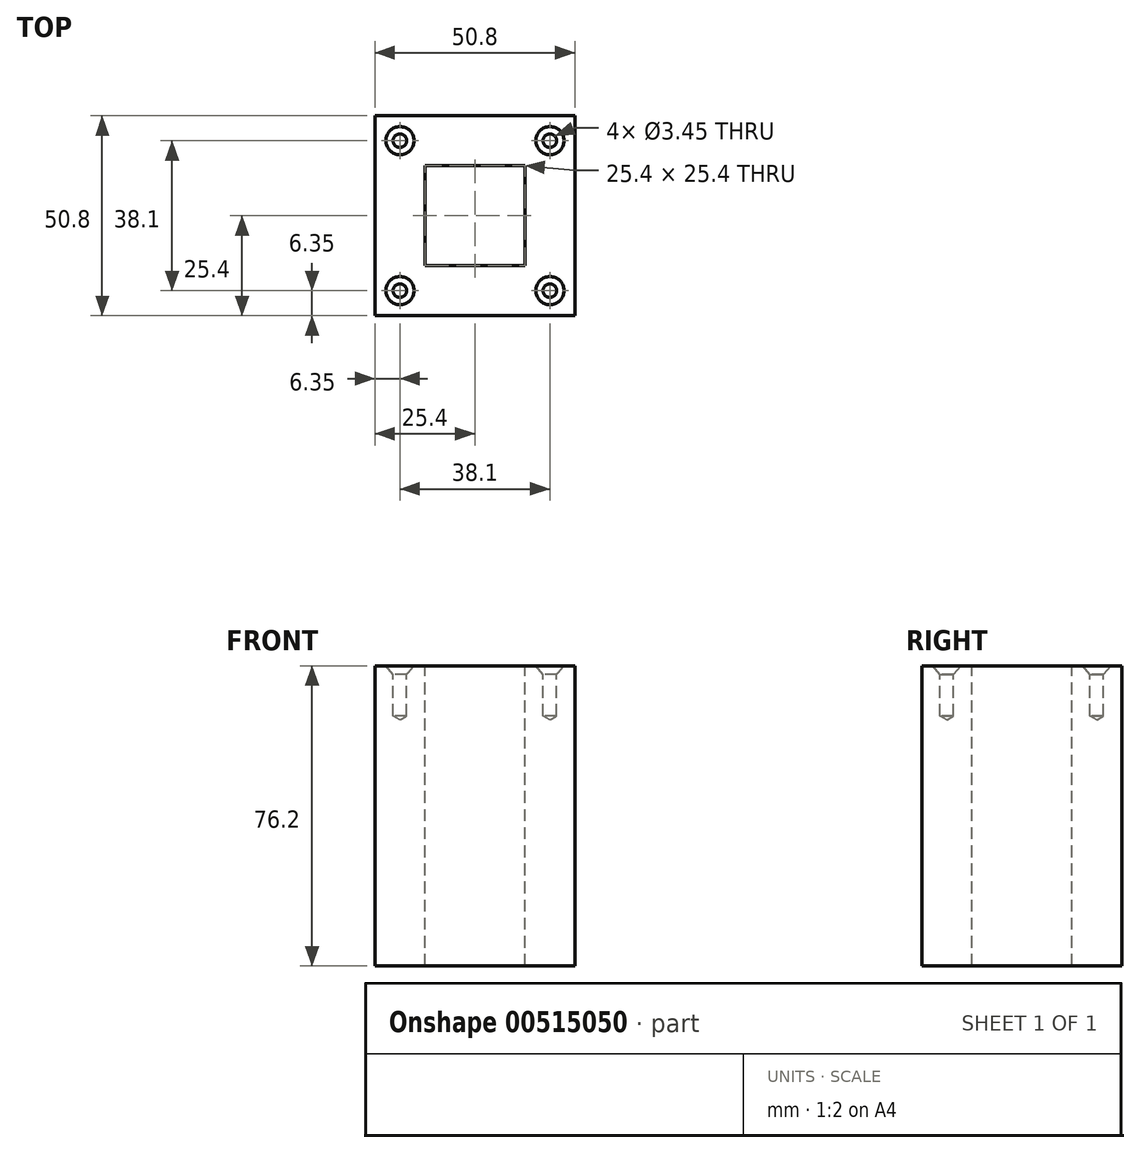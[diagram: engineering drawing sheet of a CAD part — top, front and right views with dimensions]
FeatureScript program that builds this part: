
annotation { "Feature Type Name" : "Feature", "Feature Type Description" : "" }
export const myFeature = defineFeature(function(context is Context, id is Id, definition is map)
    precondition{}
    {
        {
            var Q0;
            Q0=qCreatedBy(makeId("Top.planeOp"),FACE);
            var sketch = newSketch(context, id + "F0", { "sketchPlane" : qUnion([Q0])});
            skLineSegment(sketch, "E0.bottom", {"start": v(0, 0) * mm, "end": v(50.8, 0) * mm});
            skLineSegment(sketch, "E0.top", {"start": v(0, -50.8) * mm, "end": v(50.8, -50.8) * mm});
            skLineSegment(sketch, "E0.left", {"start": v(0, 0) * mm, "end": v(0, -50.8) * mm});
            skLineSegment(sketch, "E0.right", {"start": v(50.8, 0) * mm, "end": v(50.8, -50.8) * mm});
            skSolve(sketch);
        }
        {
            var Q0;
            Q0=makeQuery(id+"F0.imprint","IMPRINT",FACE,{"disambiguationData":[TD([[makeQuery(id+"F0.imprint","IMPRINT",EDGE,{"derivedFrom":sQuery(id+"F0.wireOp",EDGE,"E0.bottom")}),-1.0]])]});
            extrude(context, id + "F1", {"entities" : qUnion([Q0]), "depth" : 76.2 * mm, "offsetDistance" : 25.4 * mm});
        }
        {
            var Q0;
            Q0=makeQuery(id+"F1.opExtrude","CAP_FACE",FACE,{"disambiguationData":[OSD([sQuery(id+"F0.wireOp",EDGE,"E0.bottom"),sQuery(id+"F0.wireOp",EDGE,"E0.top"),sQuery(id+"F0.wireOp",EDGE,"E0.left"),sQuery(id+"F0.wireOp",EDGE,"E0.right")])],"isStart":false});
            var sketch = newSketch(context, id + "F2", { "sketchPlane" : qUnion([Q0])});
            skLineSegment(sketch, "E1.bottom", {"start": v(12.7, -12.7) * mm, "end": v(38.1, -12.7) * mm});
            skLineSegment(sketch, "E1.top", {"start": v(12.7, -38.1) * mm, "end": v(38.1, -38.1) * mm});
            skLineSegment(sketch, "E1.left", {"start": v(12.7, -12.7) * mm, "end": v(12.7, -38.1) * mm});
            skLineSegment(sketch, "E1.right", {"start": v(38.1, -12.7) * mm, "end": v(38.1, -38.1) * mm});
            skSolve(sketch);
        }
        {
            var Q0;
            Q0=makeQuery(id+"F2.imprint","IMPRINT",FACE,{"disambiguationData":[TD([[makeQuery(id+"F2.imprint","IMPRINT",EDGE,{"derivedFrom":sQuery(id+"F2.wireOp",EDGE,"E1.bottom")}),-1.0]])]});
            extrude(context, id + "F3", {"entities" : qUnion([Q0]), "operationType" : NewBodyOperationType.REMOVE, "endBound" : BoundingType.THROUGH_ALL, "oppositeDirection" : true, "depth" : 25.4 * mm, "offsetDistance" : 25.4 * mm});
        }
        {
            var Q0;
            Q0=makeQuery(id+"F1.opExtrude","CAP_FACE",FACE,{"disambiguationData":[OSD([sQuery(id+"F0.wireOp",EDGE,"E0.bottom"),sQuery(id+"F0.wireOp",EDGE,"E0.top"),sQuery(id+"F0.wireOp",EDGE,"E0.left"),sQuery(id+"F0.wireOp",EDGE,"E0.right")])],"isStart":false});
            var sketch = newSketch(context, id + "F4", { "sketchPlane" : qUnion([Q0])});
            skPoint(sketch, "E2", {"position": v(6.35, -6.35) * mm});
            skPoint(sketch, "E3", {"position": v(44.45, -6.35) * mm});
            skPoint(sketch, "E4", {"position": v(44.45, -44.45) * mm});
            skPoint(sketch, "E5", {"position": v(6.35, -44.45) * mm});
            skSolve(sketch);
        }
        {
            var Q0;
            Q0=sQuery(id+"F4.wireOp",VERTEX,"E2");
            var Q1;
            Q1=sQuery(id+"F4.wireOp",VERTEX,"E3");
            var Q2;
            Q2=sQuery(id+"F4.wireOp",VERTEX,"E4");
            var Q3;
            Q3=sQuery(id+"F4.wireOp",VERTEX,"E5");
            var Q4;
            Q4=makeQuery(id+"F1.opExtrude","SWEPT_BODY",BODY,{"disambiguationData":[OSD([sQuery(id+"F0.wireOp",EDGE,"E0.bottom"),sQuery(id+"F0.wireOp",EDGE,"E0.top"),sQuery(id+"F0.wireOp",EDGE,"E0.left"),sQuery(id+"F0.wireOp",EDGE,"E0.right")])]});
            hole(context, id + "F5", {"style" : HoleStyle.C_SINK, "endStyle" : HoleEndStyle.BLIND, "standardTappedOrClearance" : lookupTablePath({ "standard" : "ANSI", "fit" : "Normal (ASME)", "size" : "#5", "type" : "Clearance" }), "standardBlindInLast" : lookupTablePath({ "fit" : "Free", "standard" : "ANSI", "size" : "#5", "type" : "Clearance" }), "holeDiameter" : 3.45 * mm, "cSinkDiameter" : 7.14 * mm, "cSinkAngle" : 82 * degree, "holeDepth" : 12.7 * mm, "isTappedThrough" : true, "tappedDepth" : 12.7 * mm, "tapClearance" : 3, "locations" : qUnion([Q0, Q1, Q2, Q3]), "scope" : qUnion([Q4])});
        }
    });
